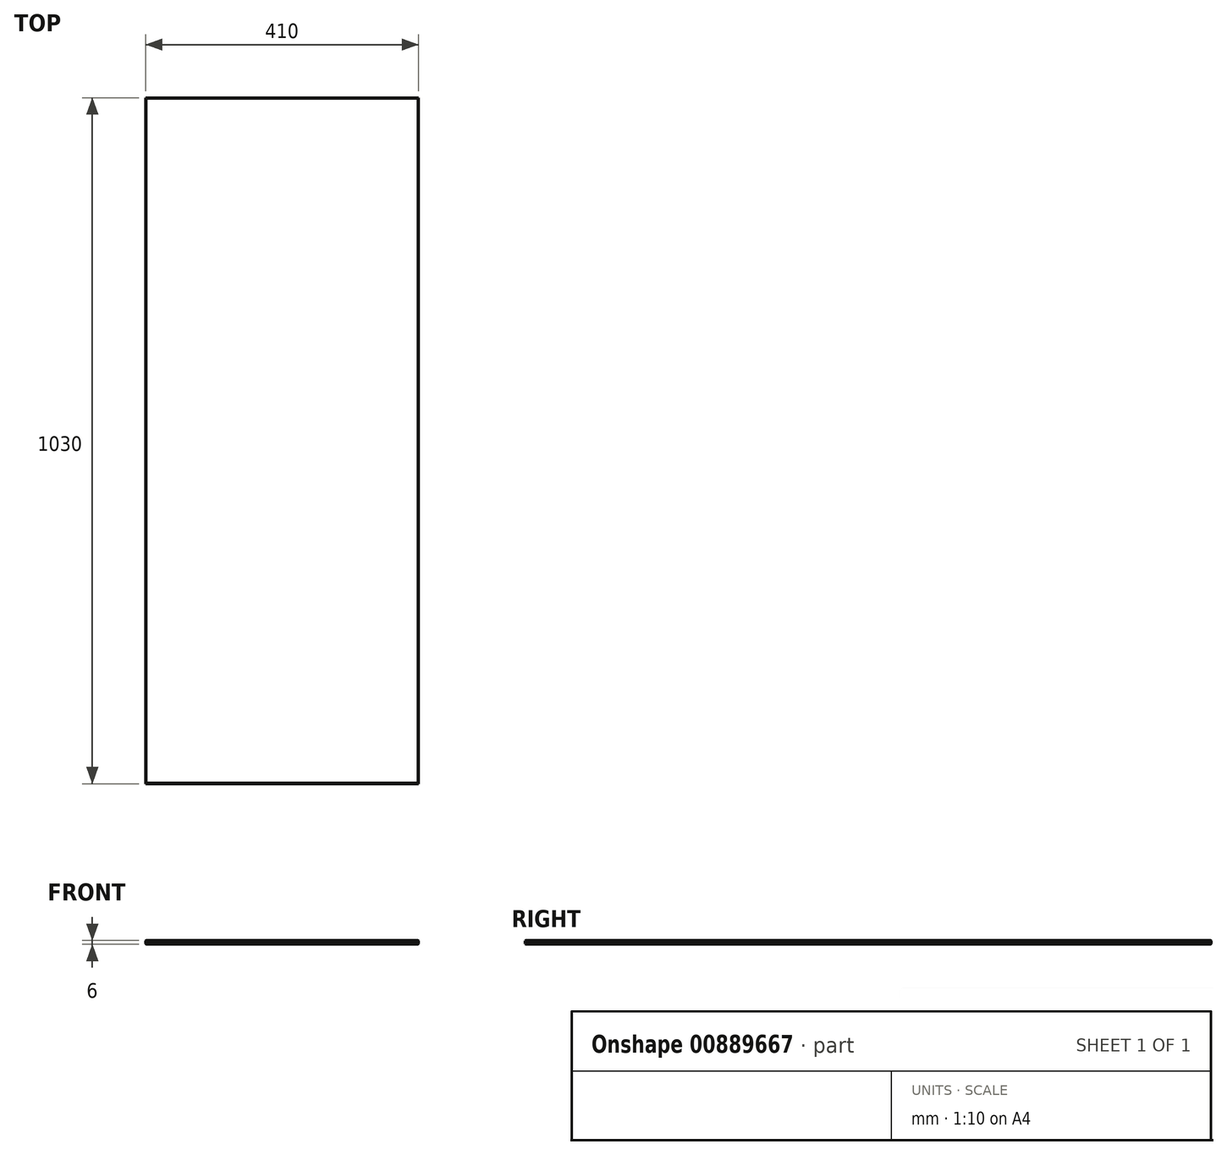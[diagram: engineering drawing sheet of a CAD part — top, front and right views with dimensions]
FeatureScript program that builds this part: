
annotation { "Feature Type Name" : "Feature", "Feature Type Description" : "" }
export const myFeature = defineFeature(function(context is Context, id is Id, definition is map)
    precondition{}
    {
        {
            var Q0;
            Q0=qCreatedBy(makeId("Top.planeOp"),FACE);
            var sketch = newSketch(context, id + "F0", { "sketchPlane" : qUnion([Q0])});
            skLineSegment(sketch, "E0.bottom", {"start": v(0, 1030) * mm, "end": v(410, 1030) * mm});
            skLineSegment(sketch, "E0.top", {"start": v(0, 0) * mm, "end": v(410, 0) * mm});
            skLineSegment(sketch, "E0.left", {"start": v(410, 1030) * mm, "end": v(410, 0) * mm});
            skLineSegment(sketch, "E0.right", {"start": v(0, 1030) * mm, "end": v(0, 0) * mm});
            skSolve(sketch);
        }
        {
            var Q0;
            Q0 = qSketchRegion(id + "F0", true);
            extrude(context, id + "F1", {"entities" : qUnion([Q0]), "depth" : 6 * mm, "offsetDistance" : 25 * mm});
        }
        {
            var Q0;
            Q0=makeQuery(id+"F1.opExtrude","CAP_EDGE",EDGE,{"disambiguationData":[OSD([sQuery(id+"F0.wireOp",EDGE,"E0.right")])],"isStart":true});
            var Q1;
            Q1=makeQuery(id+"F1.opExtrude","CAP_EDGE",EDGE,{"disambiguationData":[OSD([sQuery(id+"F0.wireOp",EDGE,"E0.top")])],"isStart":true});
            var Q2;
            Q2=makeQuery(id+"F1.opExtrude","CAP_EDGE",EDGE,{"disambiguationData":[OSD([sQuery(id+"F0.wireOp",EDGE,"E0.top")])],"isStart":false});
            var Q3;
            Q3=makeQuery(id+"F1.opExtrude","CAP_EDGE",EDGE,{"disambiguationData":[OSD([sQuery(id+"F0.wireOp",EDGE,"E0.right")])],"isStart":false});
            var Q4;
            Q4=makeQuery(id+"F1.opExtrude","CAP_FACE",FACE,{"disambiguationData":[OSD([sQuery(id+"F0.wireOp",EDGE,"E0.bottom"),sQuery(id+"F0.wireOp",EDGE,"E0.top"),sQuery(id+"F0.wireOp",EDGE,"E0.left"),sQuery(id+"F0.wireOp",EDGE,"E0.right")])],"isStart":true});
            var Q5;
            Q5=makeQuery(id+"F1.opExtrude","CAP_EDGE",EDGE,{"disambiguationData":[OSD([sQuery(id+"F0.wireOp",EDGE,"E0.bottom")])],"isStart":false});
            var Q6;
            Q6=makeQuery(id+"F1.opExtrude","CAP_EDGE",EDGE,{"disambiguationData":[OSD([sQuery(id+"F0.wireOp",EDGE,"E0.left")])],"isStart":false});
            chamfer(context, id + "F2", {"entities" : qUnion([Q0, Q1, Q2, Q3, Q4, Q5, Q6]), "width" : 1 * mm, "tangentPropagation" : true});
        }
    });
